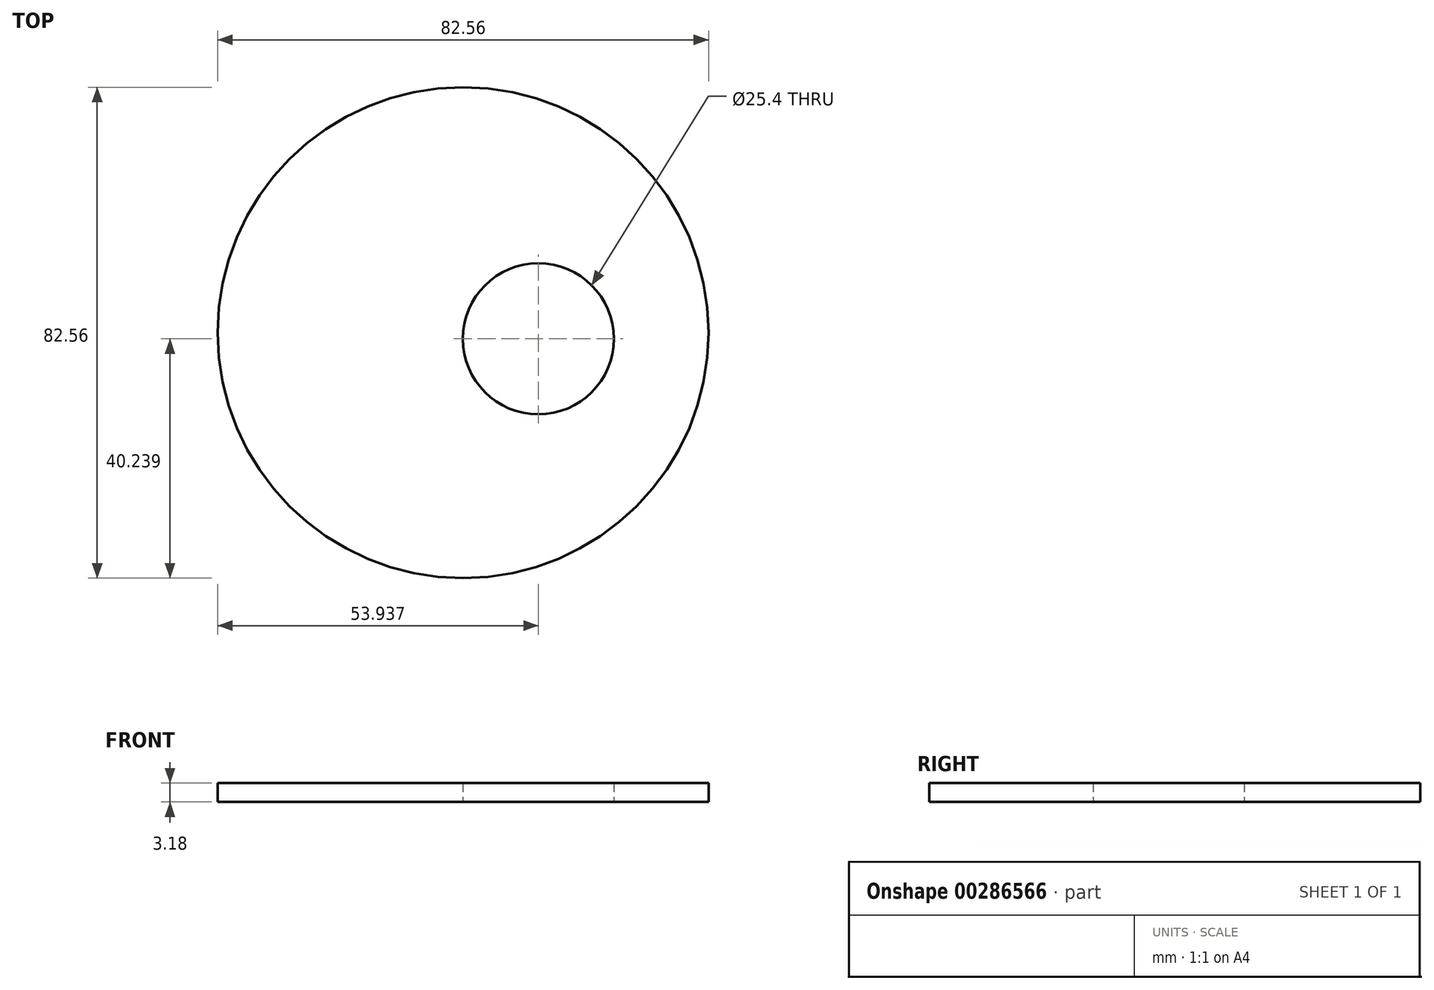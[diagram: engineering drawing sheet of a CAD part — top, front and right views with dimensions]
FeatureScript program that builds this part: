
annotation { "Feature Type Name" : "Feature", "Feature Type Description" : "" }
export const myFeature = defineFeature(function(context is Context, id is Id, definition is map)
    precondition{}
    {
        {
            var Q0;
            Q0=qCreatedBy(makeId("Top.planeOp"),FACE);
            var sketch = newSketch(context, id + "F0", { "sketchPlane" : qUnion([Q0])});
            skCircle(sketch, "E0", {"center": v(12.66, -1.04) * mm, "radius": 12.7 * mm});
            skCircle(sketch, "E1", {"center": v(0, 0) * mm, "radius": 41.27 * mm});
            skSolve(sketch);
        }
        {
            var Q0;
            Q0=makeQuery(id+"F0.imprint","IMPRINT",FACE,{"disambiguationData":[TD([[makeQuery(id+"F0.imprint","IMPRINT",EDGE,{"derivedFrom":sQuery(id+"F0.wireOp",EDGE,"E0")}),-1.0]])]});
            extrude(context, id + "F1", {"entities" : qUnion([Q0]), "depth" : 3.17 * mm});
        }
    });
